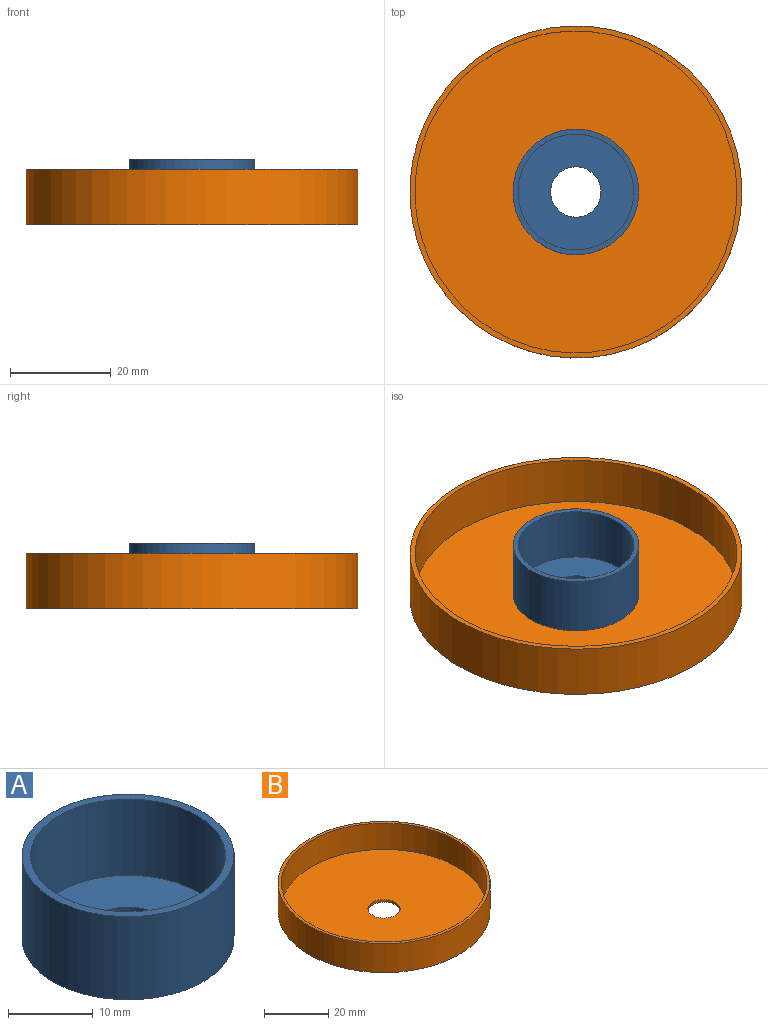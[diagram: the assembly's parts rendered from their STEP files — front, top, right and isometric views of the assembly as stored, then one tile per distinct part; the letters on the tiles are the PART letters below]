
ASSEMBLY  parts=2 mates=1
PART A: 6 faces, bbox 25x25x12 mm
  f0: cylinder r=12.5mm len=25mm, axis (0,0,-1), area 942.5mm2, adj f1,f2
  f1: plane 25x25mm, normal (0,0,1), area 75.4mm2, adj f0,f3
  f2: plane 25x25mm, normal (0,0,-1), area 412.3mm2, adj f0,f5
  f3: cylinder r=11.5mm len=23mm, axis (0,0,-1), area 794.8mm2, adj f1,f4
  f4: plane 23x23mm, normal (0,0,1), area 336.9mm2, adj f3,f5
  f5: cylinder r=5mm len=10mm, axis (0,0,-1), area 31.4mm2, adj f2,f4
PART B: 6 faces, bbox 66x66x11 mm
  f0: cylinder r=33mm len=66mm, axis (0,0,-1), area 2280.8mm2, adj f1,f2
  f1: plane 66x66mm, normal (0,0,1), area 204.2mm2, adj f0,f3
  f2: plane 66x66mm, normal (0,0,-1), area 3342.7mm2, adj f0,f5
  f3: cylinder r=32mm len=64mm, axis (0,0,-1), area 2010.6mm2, adj f1,f4
  f4: plane 64x64mm, normal (0,0,1), area 3138.5mm2, adj f3,f5
  f5: cylinder r=5mm len=10mm, axis (0,0,1), area 31.4mm2, adj f2,f4
PLACE A t=(-1.3,0.2,-3.91)mm
PLACE B t=(-1.3,0.2,-4.91)mm
MATE fastened A.f5 <-> B.f5  axis (0,0,-1) through (-1.3,0.2,-3.91)mm
